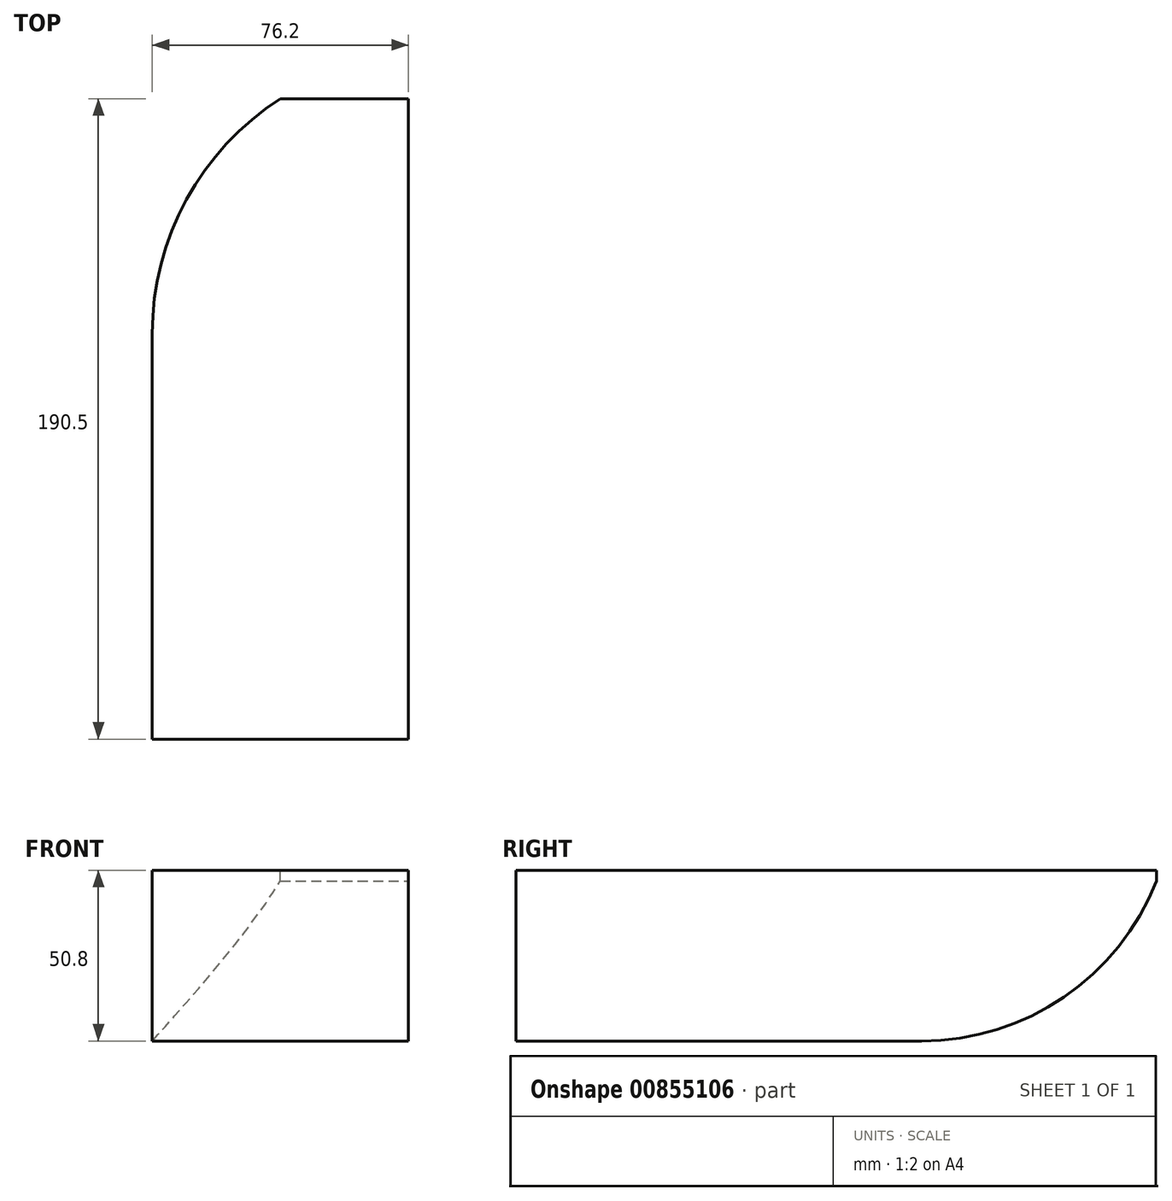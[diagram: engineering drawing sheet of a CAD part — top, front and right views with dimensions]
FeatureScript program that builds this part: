
annotation { "Feature Type Name" : "Feature", "Feature Type Description" : "" }
export const myFeature = defineFeature(function(context is Context, id is Id, definition is map)
    precondition{}
    {
        {
            var Q0;
            Q0=qCreatedBy(makeId("Front.planeOp"),FACE);
            var sketch = newSketch(context, id + "F0", { "sketchPlane" : qUnion([Q0])});
            skLineSegment(sketch, "E0.bottom", {"start": v(38.1, 25.4) * mm, "end": v(-38.1, 25.4) * mm});
            skLineSegment(sketch, "E0.top", {"start": v(38.1, -25.4) * mm, "end": v(-38.1, -25.4) * mm});
            skLineSegment(sketch, "E0.left", {"start": v(38.1, 25.4) * mm, "end": v(38.1, -25.4) * mm});
            skLineSegment(sketch, "E0.right", {"start": v(-38.1, 25.4) * mm, "end": v(-38.1, -25.4) * mm});
            skPoint(sketch, "E0.middle", {"position": v(0, 0) * mm});
            skSolve(sketch);
        }
        {
            var Q0;
            Q0 = qSketchRegion(id + "F0", true);
            extrude(context, id + "F1", {"entities" : qUnion([Q0]), "endBound" : BoundingType.SYMMETRIC, "depth" : 190.5 * mm, "offsetDistance" : 25.4 * mm});
        }
        {
            var Q0;
            Q0=qCreatedBy(makeId("Right.planeOp"),FACE);
            var sketch = newSketch(context, id + "F2", { "sketchPlane" : qUnion([Q0])});
            skLineSegment(sketch, "E1", {"start": v(95.25, 22.23) * mm, "end": v(95.25, -25.4) * mm});
            skLineSegment(sketch, "E2", {"start": v(95.25, -25.4) * mm, "end": v(25.4, -25.4) * mm});
            skArc(sketch, "E3", {"start": v(25.4, -25.4) * mm, "mid": v(67.67, -12.36) * mm, "end": v(95.25, 22.23) * mm});
            skSolve(sketch);
        }
        {
            var Q0;
            Q0 = qSketchRegion(id + "F2", true);
            extrude(context, id + "F3", {"entities" : qUnion([Q0]), "operationType" : NewBodyOperationType.REMOVE, "endBound" : BoundingType.SYMMETRIC, "oppositeDirection" : true, "depth" : 101.6 * mm, "offsetDistance" : 25.4 * mm});
        }
        {
            var Q0;
            Q0=qCreatedBy(makeId("Top.planeOp"),FACE);
            var sketch = newSketch(context, id + "F4", { "sketchPlane" : qUnion([Q0])});
            skLineSegment(sketch, "E4", {"start": v(0, 95.25) * mm, "end": v(-38.1, 95.25) * mm});
            skLineSegment(sketch, "E5", {"start": v(-38.1, 95.25) * mm, "end": v(-38.1, 25.4) * mm});
            skArc(sketch, "E6", {"start": v(0, 95.25) * mm, "mid": v(-27.96, 65.18) * mm, "end": v(-38.1, 25.4) * mm});
            skSolve(sketch);
        }
        {
            var Q0;
            Q0 = qSketchRegion(id + "F4", true);
            extrude(context, id + "F5", {"entities" : qUnion([Q0]), "operationType" : NewBodyOperationType.REMOVE, "endBound" : BoundingType.SYMMETRIC, "oppositeDirection" : true, "depth" : 76.2 * mm, "offsetDistance" : 25.4 * mm});
        }
    });
